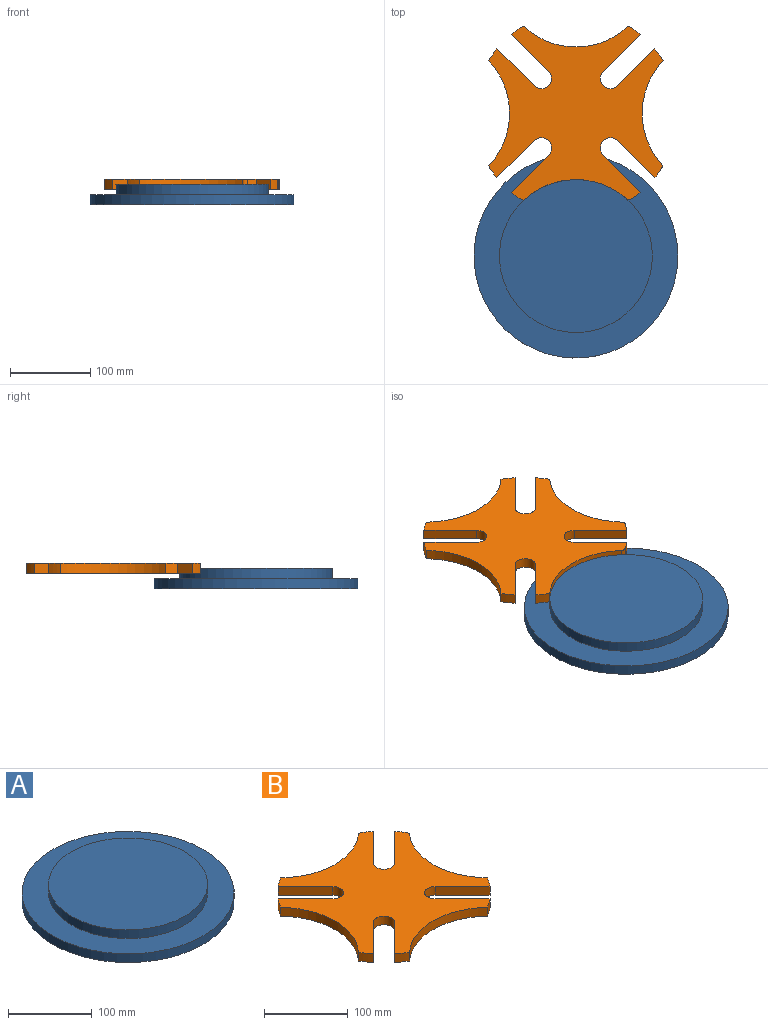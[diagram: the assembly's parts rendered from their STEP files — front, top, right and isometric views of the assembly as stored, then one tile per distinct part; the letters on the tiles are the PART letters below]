
ASSEMBLY  parts=2 mates=1
PART A: 5 faces, bbox 254x254x25.4 mm
  f0: cylinder r=127mm len=254mm, axis (0,0,-1), area 10134.1mm2, adj f1,f2
  f1: plane 254x254mm, normal (0,0,1), area 22168.5mm2, adj f0,f3
  f2: plane 254x254mm, normal (0,0,-1), area 50670.7mm2, adj f0
  f3: cylinder r=95.25mm len=190.5mm, axis (0,0,-1), area 7600.6mm2, adj f1,f4
  f4: plane 190.5x190.5mm, normal (0,0,1), area 28502.3mm2, adj f3
PART B: 28 faces, bbox 217.5x217.5x12.7 mm
  f0: cylinder r=127mm len=14.77mm, axis (0,0,-1), area 229.7mm2, adj f4,f5,f6,f27
  f1: cylinder r=127mm len=12.7mm, axis (0,0,-1), area 179.7mm2, adj f4,f5,f14,f17
  f2: cylinder r=127mm len=14.77mm, axis (0,0,-1), area 229.7mm2, adj f4,f5,f10,f21
  f3: cylinder r=127mm len=14.77mm, axis (0,0,-1), area 229.7mm2, adj f4,f5,f12,f22
  f4: plane 217.49x217.49mm, normal (0,0,1), area 27027.5mm2, adj f0,f1,f2,f3,f6,f7,f8,f9
  f5: plane 217.49x217.49mm, normal (0,0,-1), area 27027.5mm2, adj f0,f1,f2,f3,f6,f7,f8,f9
  f6: cylinder r=95.25mm len=131.21mm, axis (0,0,-1), area 1838.1mm2, adj f0,f4,f5,f13
  f7: cylinder r=127mm len=14.77mm, axis (0,0,-1), area 229.7mm2, adj f4,f5,f8,f25
  f8: cylinder r=95.25mm len=128.43mm, axis (0,0,-1), area 1790.4mm2, adj f4,f5,f7,f14
  f9: cylinder r=127mm len=12.7mm, axis (0,0,-1), area 179.7mm2, adj f4,f5,f15,f18
  f10: cylinder r=95.25mm len=128.43mm, axis (0,0,-1), area 1790.4mm2, adj f2,f4,f5,f15
  f11: cylinder r=127mm len=14.77mm, axis (0,0,-1), area 229.7mm2, adj f4,f5,f12,f19
  f12: cylinder r=95.25mm len=131.21mm, axis (0,0,-1), area 1838.1mm2, adj f3,f4,f5,f11
  f13: cylinder r=127mm len=14.77mm, axis (0,0,-1), area 229.7mm2, adj f4,f5,f6,f23
  f14: cylinder r=5.08mm len=12.7mm, axis (0,0,1), area 83.5mm2, adj f1,f4,f5,f8
  f15: cylinder r=5.08mm len=12.7mm, axis (0,0,1), area 83.5mm2, adj f4,f5,f9,f10
  f16: cylinder r=12.7mm len=21.68mm, axis (0,0,1), area 506.7mm2, adj f4,f5,f17,f18
  f17: plane 46.25x46.25mm, normal (-0.71,0.71,0), area 830.6mm2, adj f1,f4,f5,f16
  f18: plane 46.25x46.25mm, normal (0.71,-0.71,0), area 830.6mm2, adj f4,f5,f9,f16
  f19: plane 46.25x46.25mm, normal (0.71,0.71,0), area 830.6mm2, adj f4,f5,f11,f20
  f20: cylinder r=12.7mm len=21.68mm, axis (0,0,1), area 506.7mm2, adj f4,f5,f19,f21
  f21: plane 46.25x46.25mm, normal (-0.71,-0.71,0), area 830.6mm2, adj f2,f4,f5,f20
  f22: plane 46.25x46.25mm, normal (0.71,-0.71,0), area 830.6mm2, adj f3,f4,f5,f24
  f23: plane 46.25x46.25mm, normal (-0.71,0.71,0), area 830.6mm2, adj f4,f5,f13,f24
  f24: cylinder r=12.7mm len=21.68mm, axis (0,0,1), area 506.7mm2, adj f4,f5,f22,f23
  f25: plane 46.25x46.25mm, normal (-0.71,-0.71,0), area 830.6mm2, adj f4,f5,f7,f26
  f26: cylinder r=12.7mm len=21.68mm, axis (0,0,1), area 506.7mm2, adj f4,f5,f25,f27
  f27: plane 46.25x46.25mm, normal (0.71,0.71,0), area 830.6mm2, adj f0,f4,f5,f26
PLACE A t=(-205.01,0.58,-73.41)mm
PLACE B rot(axis=(0,0,-1),90deg) t=(-205.01,178.38,-54.36)mm
MATE revolute B.f8 <-> A.f0  axis (0,0,-1) through (-205.01,0.58,-48.01)mm
